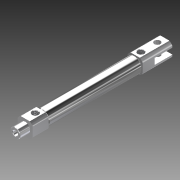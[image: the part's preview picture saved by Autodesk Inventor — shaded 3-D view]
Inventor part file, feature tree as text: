
AUTODESK INVENTOR PART (.ipt)
format: ipt  version: 2012 (Build 160160000, 160)  size: 160,768 bytes
history: native  units: in
note: dims shown in document units (in); Inventor stores cm internally (conversion verified against a paired STEP export)
features: thread x2, other x1, imported_body x1, hole x1, sketch x1
ambient origin geometry x8: Origin, YZ Plane, XZ Plane, XY Plane, X Axis, Y Axis, Z Axis, Center Point
feature tree (6):
  parser-record x1  (decoder bookkeeping rows leaked as tree rows — omitted from the tree; the rows remain in map.json)
  imported_body  "Base1"
  thread  "Thread1"  [1 undecoded]
  thread  "Thread2"  [1 undecoded]
  hole  "Hole1"  [1 undecoded]
  sketch  "Sketch1"  dims[d4=0.1882in d5=0.2362in d6=0.1575in d7=0.0787in d8=90.0deg d9=0.315in d10=0.8108in]
note: 3 required parameter values undecoded (feature->parameter linkage not recoverable at this tier; creation-order binding heuristic only, values carry confidence <= 0.55)
